# Revit family: Längsverbinder, Seitenhöhe 110- LVG 110 FS,FT,FT SO,A2,A4
name_source: partatom
category: Generic Models
revit_build: Autodesk Revit 2017 (Build: 20190508_0315(x64)
units: mm (PartAtom-declared; Revit-internal decimal feet)

## family parameters
Always vertical = Yes
Can host rebar = No
Cut with Voids When Loaded = No
Part Type = Normal
Room Calculation Point = No
Round Connector Dimension = Use Diameter
Shared = No
Work Plane-Based = No

## types (5) — shared parameters
Height = 114 mm  [stored 0.374016 ft]
Height 1 = 157 mm  [stored 0.515092 ft]
Manufacturer = OBO Bettermann
URL = http://www.obo-bettermann.com
Width = 250 mm  [stored 0.82021 ft]
Width 1 = 125 mm  [stored 0.410105 ft]

## per-type parameters (varying)
| type | GTIN | Manufacturer Art.No. | Material |
| LVG 110 FT | 4012195065685 | 6216548 | Hot-dip galvanised |
| LVG 110 FT SO | 4012195652267 | 7189256 | Hot-dip galvanised 85 µm |
| LVG 110 FS | 4012195065678 | 6216545 | Strip-galvanised |
| LVG 110 A2 | 4012195623885 | 6216550 | Stainless steel, A2 |
| LVG 110 A4 | 4012196129362 | 6216551 | Stainless steel, A4 |

note: column(s) folded — value = type name in every type: Article Type

note: [stored X ft] marks values corroborated as IEEE doubles in the binary element streams (Revit-internal decimal feet)

## geometry (parser evidence)
native form markers: Sweep x2
no freeform markers — native parametric forms only
